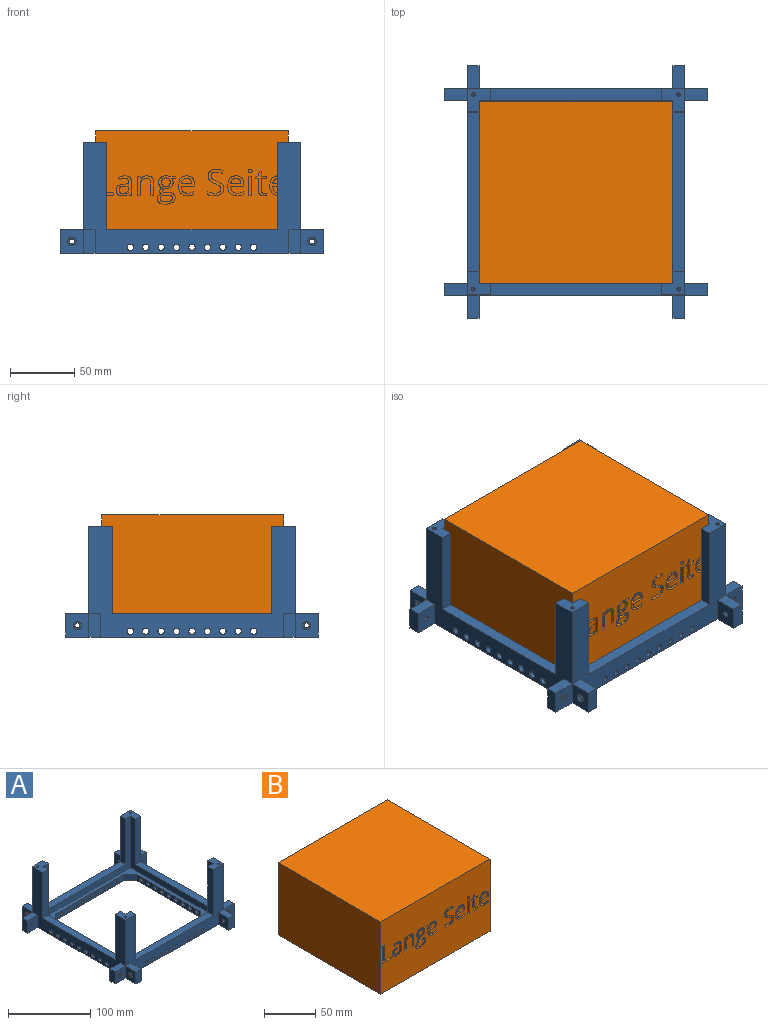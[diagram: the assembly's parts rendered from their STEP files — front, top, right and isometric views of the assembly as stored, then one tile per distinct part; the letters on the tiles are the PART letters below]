
ASSEMBLY  parts=2 mates=1
PART A: 142 faces, bbox 205x196.5x86 mm
  f0: plane 20.61x9mm, normal (0,1,0), area 185.5mm2, adj f1,f16,f33,f129
  f1: plane 142.5x77mm, normal (-1,0,0), area 2417.1mm2, adj f0,f16,f51,f53,f54,f67,f68,f70
  f2: cylinder r=2mm len=7mm, axis (-1,0,0), area 88mm2, adj f27,f90
  f3: cylinder r=2mm len=7mm, axis (0,-1,0), area 88mm2, adj f32,f88
  f4: cylinder r=2mm len=7mm, axis (0,-1,0), area 88mm2, adj f34,f86
  f5: cylinder r=2mm len=7mm, axis (1,0,0), area 88mm2, adj f39,f84
  f6: cylinder r=2mm len=7mm, axis (0,-1,0), area 88mm2, adj f46,f82
  f7: cylinder r=2mm len=7mm, axis (1,0,0), area 88mm2, adj f41,f80
  f8: cylinder r=2mm len=7mm, axis (-1,0,0), area 88mm2, adj f25,f78
  f9: cylinder r=2mm len=7mm, axis (0,-1,0), area 88mm2, adj f48,f76
  f10: plane 133x9mm, normal (0,0,1), area 1197mm2, adj f40,f51,f69,f72
  f11: plane 124.5x9mm, normal (0,0,1), area 1120.5mm2, adj f47,f52,f63,f73
  f12: plane 18x9mm, normal (0,0,1), area 162mm2, adj f44,f45,f46,f47
  f13: plane 18x9mm, normal (0,0,1), area 162mm2, adj f40,f41,f42,f43
  f14: plane 18x9mm, normal (0,0,1), area 162mm2, adj f37,f38,f39,f40
  f15: plane 18x9mm, normal (0,0,1), area 162mm2, adj f33,f34,f35,f36
  f16: plane 124.5x9mm, normal (0,0,1), area 1120.5mm2, adj f0,f1,f33,f70
  f17: plane 133x9mm, normal (0,0,1), area 1197mm2, adj f26,f53,f64,f66
  f18: plane 18x9mm, normal (0,0,1), area 162mm2, adj f30,f31,f32,f33
  f19: plane 18x9mm, normal (0,0,1), area 162mm2, adj f26,f27,f28,f29
  f20: plane 18x9mm, normal (0,0,1), area 162mm2, adj f23,f24,f25,f26
  f21: plane 18x9mm, normal (0,0,1), area 162mm2, adj f22,f47,f48,f49
  f22: plane 18x18mm, normal (0,-1,0), area 290.8mm2, adj f21,f23,f49,f50,f75
  f23: plane 18x18mm, normal (-1,0,0), area 290.8mm2, adj f20,f22,f24,f50,f77
  f24: plane 18x9mm, normal (0,-1,0), area 162mm2, adj f20,f23,f25,f50
  f25: plane 18x18mm, normal (1,0,0), area 311.4mm2, adj f8,f20,f24,f26,f50
  f26: plane 169x86mm, normal (0,-1,0), area 4989.3mm2, adj f17,f19,f20,f25,f27,f33,f47,f50
  f27: plane 18x18mm, normal (-1,0,0), area 311.4mm2, adj f2,f19,f26,f28,f50
  f28: plane 18x9mm, normal (0,-1,0), area 162mm2, adj f19,f27,f29,f50
  f29: plane 18x18mm, normal (1,0,0), area 290.8mm2, adj f19,f28,f30,f50,f89
  f30: plane 18x18mm, normal (0,-1,0), area 290.8mm2, adj f18,f29,f31,f50,f87
  f31: plane 18x9mm, normal (1,0,0), area 162mm2, adj f18,f30,f32,f50
  f32: plane 18x18mm, normal (0,1,0), area 311.4mm2, adj f3,f18,f31,f33,f50
  f33: plane 160.5x86mm, normal (1,0,0), area 4746.9mm2, adj f0,f15,f16,f18,f26,f32,f34,f40
  f34: plane 18x18mm, normal (0,-1,0), area 311.4mm2, adj f4,f15,f33,f35,f50
  f35: plane 18x9mm, normal (1,0,0), area 162mm2, adj f15,f34,f36,f50
  f36: plane 18x18mm, normal (0,1,0), area 290.8mm2, adj f15,f35,f37,f50,f85
  f37: plane 18x18mm, normal (1,0,0), area 290.8mm2, adj f14,f36,f38,f50,f83
  f38: plane 18x9mm, normal (0,1,0), area 162mm2, adj f14,f37,f39,f50
  f39: plane 18x18mm, normal (-1,0,0), area 311.4mm2, adj f5,f14,f38,f40,f50
  f40: plane 169x86mm, normal (0,1,0), area 4989.3mm2, adj f10,f13,f14,f33,f39,f41,f47,f50
  f41: plane 18x18mm, normal (1,0,0), area 311.4mm2, adj f7,f13,f40,f42,f50
  f42: plane 18x9mm, normal (0,1,0), area 162mm2, adj f13,f41,f43,f50
  f43: plane 18x18mm, normal (-1,0,0), area 290.8mm2, adj f13,f42,f44,f50,f79
  f44: plane 18x18mm, normal (0,1,0), area 290.8mm2, adj f12,f43,f45,f50,f81
  f45: plane 18x9mm, normal (-1,0,0), area 162mm2, adj f12,f44,f46,f50
  f46: plane 18x18mm, normal (0,-1,0), area 311.4mm2, adj f6,f12,f45,f47,f50
  f47: plane 160.5x86mm, normal (-1,0,0), area 4836.3mm2, adj f11,f12,f21,f26,f40,f46,f48,f50
  f48: plane 18x18mm, normal (0,1,0), area 311.4mm2, adj f9,f21,f47,f49,f50
  f49: plane 18x9mm, normal (-1,0,0), area 162mm2, adj f21,f22,f48,f50
  f50: plane 205x196.5mm, normal (0,0,-1), area 9989.5mm2, adj f22,f23,f24,f25,f26,f27,f28,f29
  f51: plane 151x77mm, normal (0,-1,0), area 2583mm2, adj f1,f10,f52,f54,f69,f71,f72,f74
  f52: plane 142.5x77mm, normal (1,0,0), area 2506.5mm2, adj f11,f51,f53,f54,f63,f65,f73,f74
  f53: plane 151x77mm, normal (0,1,0), area 2583mm2, adj f1,f17,f52,f54,f64,f65,f66,f68
  f54: plane 151x142.5mm, normal (0,0,1), area 3086.5mm2, adj f1,f51,f52,f53,f55,f56,f57,f58
  f55: plane 11.21x11.21mm, normal (0.71,-0.71,0), area 142.7mm2, adj f50,f54,f56,f62
  f56: plane 110.07x9mm, normal (1,0,0), area 813.9mm2, adj f50,f54,f55,f57,f100,f101,f102,f103
  f57: plane 11.21x11.21mm, normal (0.71,0.71,0), area 142.7mm2, adj f50,f54,f56,f58
  f58: plane 118.57x9mm, normal (0,1,0), area 890.4mm2, adj f50,f54,f57,f59,f118,f119,f120,f121
  f59: plane 11.21x11.21mm, normal (-0.71,0.71,0), area 142.7mm2, adj f50,f54,f58,f60
  f60: plane 110.07x9mm, normal (-1,0,0), area 813.9mm2, adj f50,f54,f59,f61,f91,f92,f93,f94
  f61: plane 11.21x11.21mm, normal (-0.71,-0.71,0), area 142.7mm2, adj f50,f54,f60,f62
  f62: plane 118.57x9mm, normal (0,-1,0), area 890.4mm2, adj f50,f54,f55,f61,f109,f110,f111,f112
  f63: plane 68x9mm, normal (0,1,0), area 612mm2, adj f11,f47,f52,f65
  f64: plane 68x9mm, normal (1,0,0), area 612mm2, adj f17,f26,f53,f65
  f65: plane 18x18mm, normal (0,0,1), area 235.9mm2, adj f26,f47,f52,f53,f63,f64,f131
  f66: plane 68x9mm, normal (-1,0,0), area 612mm2, adj f17,f26,f53,f68
  f67: plane 26.61x9mm, normal (0,1,0), area 239.5mm2, adj f1,f33,f68,f127
  f68: plane 18x18mm, normal (0,0,1), area 235.9mm2, adj f1,f26,f33,f53,f66,f67,f134
  f69: plane 68x9mm, normal (-1,0,0), area 612mm2, adj f10,f40,f51,f71
  f70: plane 68x9mm, normal (0,-1,0), area 612mm2, adj f1,f16,f33,f71
  f71: plane 18x18mm, normal (0,0,1), area 235.9mm2, adj f1,f33,f40,f51,f69,f70,f137
  f72: plane 68x9mm, normal (1,0,0), area 612mm2, adj f10,f40,f51,f74
  f73: plane 68x9mm, normal (0,-1,0), area 612mm2, adj f11,f47,f52,f74
  f74: plane 18x18mm, normal (0,0,1), area 235.9mm2, adj f40,f47,f51,f52,f72,f73,f140
  f75: cylinder r=3.25mm len=6.5mm, axis (0,-1,0), area 40.8mm2, adj f22,f76
  f76: plane 6.5x6.5mm, normal (0,-1,0), area 20.6mm2, adj f9,f75
  f77: cylinder r=3.25mm len=6.5mm, axis (-1,0,0), area 40.8mm2, adj f23,f78
  f78: plane 6.5x6.5mm, normal (-1,0,0), area 20.6mm2, adj f8,f77
  f79: cylinder r=3.25mm len=6.5mm, axis (-1,0,0), area 40.8mm2, adj f43,f80
  f80: plane 6.5x6.5mm, normal (-1,0,0), area 20.6mm2, adj f7,f79
  f81: cylinder r=3.25mm len=6.5mm, axis (0,1,0), area 40.8mm2, adj f44,f82
  f82: plane 6.5x6.5mm, normal (0,1,0), area 20.6mm2, adj f6,f81
  f83: cylinder r=3.25mm len=6.5mm, axis (1,0,0), area 40.8mm2, adj f37,f84
  f84: plane 6.5x6.5mm, normal (1,0,0), area 20.6mm2, adj f5,f83
  f85: cylinder r=3.25mm len=6.5mm, axis (0,1,0), area 40.8mm2, adj f36,f86
  f86: plane 6.5x6.5mm, normal (0,1,0), area 20.6mm2, adj f4,f85
  f87: cylinder r=3.25mm len=6.5mm, axis (0,-1,0), area 40.8mm2, adj f30,f88
  f88: plane 6.5x6.5mm, normal (0,-1,0), area 20.6mm2, adj f3,f87
  f89: cylinder r=3.25mm len=6.5mm, axis (1,0,0), area 40.8mm2, adj f29,f90
  f90: plane 6.5x6.5mm, normal (1,0,0), area 20.6mm2, adj f2,f89
  f91: cylinder r=2.5mm len=14mm, axis (1,0,0), area 219.9mm2, adj f33,f60
  f92: cylinder r=2.5mm len=14mm, axis (1,0,0), area 219.9mm2, adj f33,f60
  f93: cylinder r=2.5mm len=14mm, axis (1,0,0), area 219.9mm2, adj f33,f60
  f94: cylinder r=2.5mm len=14mm, axis (1,0,0), area 219.9mm2, adj f33,f60
  f95: cylinder r=2.5mm len=14mm, axis (1,0,0), area 219.9mm2, adj f33,f60
  f96: cylinder r=2.5mm len=14mm, axis (1,0,0), area 219.9mm2, adj f33,f60
  f97: cylinder r=2.5mm len=14mm, axis (1,0,0), area 219.9mm2, adj f33,f60
  f98: cylinder r=2.5mm len=14mm, axis (1,0,0), area 219.9mm2, adj f33,f60
  f99: cylinder r=2.5mm len=14mm, axis (1,0,0), area 219.9mm2, adj f33,f60
  f100: cylinder r=2.5mm len=14mm, axis (1,0,0), area 219.9mm2, adj f47,f56
  f101: cylinder r=2.5mm len=14mm, axis (1,0,0), area 219.9mm2, adj f47,f56
  f102: cylinder r=2.5mm len=14mm, axis (1,0,0), area 219.9mm2, adj f47,f56
  f103: cylinder r=2.5mm len=14mm, axis (1,0,0), area 219.9mm2, adj f47,f56
  f104: cylinder r=2.5mm len=14mm, axis (1,0,0), area 219.9mm2, adj f47,f56
  f105: cylinder r=2.5mm len=14mm, axis (1,0,0), area 219.9mm2, adj f47,f56
  f106: cylinder r=2.5mm len=14mm, axis (1,0,0), area 219.9mm2, adj f47,f56
  f107: cylinder r=2.5mm len=14mm, axis (1,0,0), area 219.9mm2, adj f47,f56
  f108: cylinder r=2.5mm len=14mm, axis (1,0,0), area 219.9mm2, adj f47,f56
  f109: cylinder r=2.5mm len=14mm, axis (0,-1,0), area 219.9mm2, adj f40,f62
  f110: cylinder r=2.5mm len=14mm, axis (0,-1,0), area 219.9mm2, adj f40,f62
  f111: cylinder r=2.5mm len=14mm, axis (0,-1,0), area 219.9mm2, adj f40,f62
  f112: cylinder r=2.5mm len=14mm, axis (0,-1,0), area 219.9mm2, adj f40,f62
  f113: cylinder r=2.5mm len=14mm, axis (0,-1,0), area 219.9mm2, adj f40,f62
  f114: cylinder r=2.5mm len=14mm, axis (0,-1,0), area 219.9mm2, adj f40,f62
  f115: cylinder r=2.5mm len=14mm, axis (0,-1,0), area 219.9mm2, adj f40,f62
  f116: cylinder r=2.5mm len=14mm, axis (0,-1,0), area 219.9mm2, adj f40,f62
  f117: cylinder r=2.5mm len=14mm, axis (0,-1,0), area 219.9mm2, adj f40,f62
  f118: cylinder r=2.5mm len=14mm, axis (0,-1,0), area 219.9mm2, adj f26,f58
  f119: cylinder r=2.5mm len=14mm, axis (0,-1,0), area 219.9mm2, adj f26,f58
  f120: cylinder r=2.5mm len=14mm, axis (0,-1,0), area 219.9mm2, adj f26,f58
  f121: cylinder r=2.5mm len=14mm, axis (0,-1,0), area 219.9mm2, adj f26,f58
  f122: cylinder r=2.5mm len=14mm, axis (0,-1,0), area 219.9mm2, adj f26,f58
  f123: cylinder r=2.5mm len=14mm, axis (0,-1,0), area 219.9mm2, adj f26,f58
  f124: cylinder r=2.5mm len=14mm, axis (0,-1,0), area 219.9mm2, adj f26,f58
  f125: cylinder r=2.5mm len=14mm, axis (0,-1,0), area 219.9mm2, adj f26,f58
  f126: cylinder r=2.5mm len=14mm, axis (0,-1,0), area 219.9mm2, adj f26,f58
  f127: plane 9x5mm, normal (0,0.5,-0.87), area 52mm2, adj f1,f33,f67,f128
  f128: plane 15x9mm, normal (0,1,0), area 135mm2, adj f1,f33,f127,f129
  f129: plane 9x5mm, normal (0,0.5,0.87), area 52mm2, adj f0,f1,f33,f128
  f130: cylinder r=1.25mm len=11.75mm, axis (0,0,1), area 92.3mm2, adj f131,f132
  f131: cone r=1.25mm half-angle=45deg, axis (0,0,1), area 3.1mm2, adj f65,f130
  f132: cone r=0mm half-angle=59deg, axis (0,0,1), area 5.7mm2, adj f130
  f133: cylinder r=1.25mm len=11.75mm, axis (0,0,1), area 92.3mm2, adj f134,f135
  f134: cone r=1.25mm half-angle=45deg, axis (0,0,1), area 3.1mm2, adj f68,f133
  f135: cone r=0mm half-angle=59deg, axis (0,0,1), area 5.7mm2, adj f133
  f136: cylinder r=1.25mm len=11.75mm, axis (0,0,1), area 92.3mm2, adj f137,f138
  f137: cone r=1.25mm half-angle=45deg, axis (0,0,1), area 3.1mm2, adj f71,f136
  f138: cone r=0mm half-angle=59deg, axis (0,0,1), area 5.7mm2, adj f136
  f139: cylinder r=1.25mm len=11.75mm, axis (0,0,1), area 92.3mm2, adj f140,f141
  f140: cone r=1.25mm half-angle=45deg, axis (0,0,1), area 3.1mm2, adj f74,f139
  f141: cone r=0mm half-angle=59deg, axis (0,0,1), area 5.7mm2, adj f139
PART B: 230 faces, bbox 150x141.5x86 mm
  f0: plane 150x86mm, normal (0,-1,0), area 11875mm2, adj f1,f2,f4,f5,f6,f7,f8,f9
  f1: plane 141.5x86mm, normal (-1,0,0), area 12169mm2, adj f0,f3,f4,f5
  f2: plane 141.5x86mm, normal (1,0,0), area 12169mm2, adj f0,f3,f4,f5
  f3: plane 150x86mm, normal (0,1,0), area 12900mm2, adj f1,f2,f4,f5
  f4: plane 150x141.5mm, normal (0,0,1), area 21225mm2, adj f0,f1,f2,f3
  f5: plane 150x141.5mm, normal (0,0,-1), area 21225mm2, adj f0,f1,f2,f3
  f6: extruded ~3x1.17mm, area 3.5mm2, adj f0,f7,f24,f25
  f7: extruded ~3x1.77mm, area 5.9mm2, adj f0,f6,f8,f25
  f8: extruded ~3x2.08mm, area 6.7mm2, adj f0,f7,f9,f25
  f9: plane 8.84x3mm, normal (-1,0,0), area 26.5mm2, adj f0,f8,f10,f25
  f10: plane 4.36x3mm, normal (0,0,1), area 13.1mm2, adj f0,f9,f11,f25
  f11: plane 3x1.77mm, normal (-1,0,0), area 5.3mm2, adj f0,f10,f12,f25
  f12: plane 4.36x3mm, normal (0,0,-1), area 13.1mm2, adj f0,f11,f13,f25
  f13: plane 3.48x3mm, normal (-1,0,0), area 10.4mm2, adj f0,f12,f14,f25
  f14: plane 3x1.32mm, normal (0,0,-1), area 3.9mm2, adj f0,f13,f15,f25
  f15: plane 3.2x3mm, normal (0.96,0,-0.29), area 10mm2, adj f0,f14,f16,f25
  f16: plane 3x2.15mm, normal (0.4,0,-0.92), area 7.1mm2, adj f0,f15,f17,f25
  f17: plane 3x1.1mm, normal (1,0,0), area 3.3mm2, adj f0,f16,f18,f25
  f18: plane 3x2.15mm, normal (0,0,1), area 6.5mm2, adj f0,f17,f19,f25
  f19: plane 8.93x3mm, normal (1,0,0), area 26.8mm2, adj f0,f18,f20,f25
  f20: extruded ~4.59x4.35mm, area 21.8mm2, adj f0,f19,f21,f25
  f21: extruded ~3x1.3mm, area 3.9mm2, adj f0,f20,f22,f25
  f22: extruded ~3x1.09mm, area 3.4mm2, adj f0,f21,f23,f25
  f23: plane 3x1.74mm, normal (-1,0,0), area 5.2mm2, adj f0,f22,f24,f25
  f24: extruded ~3x0.89mm, area 2.7mm2, adj f0,f6,f23,f25
  f25: plane 18.77x8.89mm, normal (0,-1,0), area 58.3mm2, adj f6,f7,f8,f9,f10,f11,f12,f13
  f26: extruded ~3.34x3mm, area 10.9mm2, adj f27,f52,f53,f225
  f27: extruded ~3x2.09mm, area 6.7mm2, adj f26,f28,f53,f225
  f28: extruded ~3x1.88mm, area 6.3mm2, adj f27,f29,f53,f225
  f29: extruded ~3x2.32mm, area 8.2mm2, adj f28,f30,f53,f225
  f30: extruded ~3.91x3mm, area 12.1mm2, adj f29,f31,f53,f225
  f31: plane 3x2.28mm, normal (-0.04,0,1), area 6.8mm2, adj f30,f32,f53,f225
  f32: plane 3x1.35mm, normal (1,0,0), area 4.1mm2, adj f31,f52,f53,f225
  f33: plane 3x2.14mm, normal (0.98,0,0.21), area 6.6mm2, adj f0,f34,f51,f53
  f34: plane 3x1.69mm, normal (0,0,1), area 5.1mm2, adj f0,f33,f35,f53
  f35: plane 10.25x3mm, normal (-1,0,0), area 30.7mm2, adj f0,f34,f36,f53
  f36: extruded ~3.82x3mm, area 12.5mm2, adj f0,f35,f37,f53
  f37: extruded ~3.98x3mm, area 12.7mm2, adj f0,f36,f38,f53
  f38: extruded ~3x2.65mm, area 8mm2, adj f0,f37,f39,f53
  f39: extruded ~3x2.43mm, area 7.8mm2, adj f0,f38,f40,f53
  f40: plane 3x1.74mm, normal (0.93,0,0.37), area 5.6mm2, adj f0,f39,f41,f53
  f41: extruded ~4.24x3mm, area 13.3mm2, adj f0,f40,f42,f53
  f42: extruded ~3x2.43mm, area 8mm2, adj f0,f41,f43,f53
  f43: extruded ~3x2.61mm, area 8.3mm2, adj f0,f42,f44,f53
  f44: plane 3x0.93mm, normal (1,0,0), area 2.8mm2, adj f0,f43,f45,f53
  f45: plane 3x2.55mm, normal (0.03,0,-1), area 7.6mm2, adj f0,f44,f46,f53
  f46: extruded ~7.27x4.76mm, area 29.3mm2, adj f0,f45,f47,f53
  f47: extruded ~3.27x3mm, area 10.9mm2, adj f0,f46,f48,f53
  f48: extruded ~3.5x3mm, area 11.3mm2, adj f0,f47,f49,f53
  f49: extruded ~3x2.79mm, area 8.6mm2, adj f0,f48,f50,f53
  f50: extruded ~3x2.24mm, area 8.9mm2, adj f0,f49,f51,f53
  f51: plane 3x0.11mm, normal (0,0,1), area 0.3mm2, adj f0,f33,f50,f53
  f52: extruded ~3.26x3mm, area 10.7mm2, adj f26,f32,f53,f225
  f53: plane 15.53x12.04mm, normal (0,-1,0), area 88.3mm2, adj f26,f27,f28,f29,f30,f31,f32,f33
  f54: extruded ~3x2.88mm, area 9.6mm2, adj f55,f72,f73,f226
  f55: extruded ~3x2.74mm, area 9.2mm2, adj f54,f56,f73,f226
  f56: extruded ~3.29x3mm, area 10.5mm2, adj f55,f57,f73,f226
  f57: plane 7.85x3mm, normal (0,0,-1), area 23.6mm2, adj f56,f72,f73,f226
  f58: extruded ~5.25x3mm, area 17.4mm2, adj f0,f59,f71,f73
  f59: extruded ~3x2.6mm, area 7.8mm2, adj f0,f58,f60,f73
  f60: extruded ~3x2.28mm, area 7.2mm2, adj f0,f59,f61,f73
  f61: plane 3x2.03mm, normal (-1,0,0), area 6.1mm2, adj f0,f60,f62,f73
  f62: extruded ~4.79x3mm, area 14.8mm2, adj f0,f61,f63,f73
  f63: extruded ~3.57x3mm, area 11.8mm2, adj f0,f62,f64,f73
  f64: extruded ~4.01x3mm, area 13mm2, adj f0,f63,f65,f73
  f65: plane 10.34x3mm, normal (0,0,1), area 31mm2, adj f0,f64,f66,f73
  f66: plane 3x1.44mm, normal (-1,0,0), area 4.3mm2, adj f0,f65,f67,f73
  f67: extruded ~4.9x3mm, area 15.9mm2, adj f0,f66,f68,f73
  f68: extruded ~4.46x3mm, area 15mm2, adj f0,f67,f69,f73
  f69: extruded ~4.8x3mm, area 16.3mm2, adj f0,f68,f70,f73
  f70: extruded ~5.77x3mm, area 18.5mm2, adj f0,f69,f71,f73
  f71: extruded ~5.63x3mm, area 18.3mm2, adj f0,f58,f70,f73
  f72: extruded ~3.26x3mm, area 10.7mm2, adj f54,f57,f73,f226
  f73: plane 15.56x12.7mm, normal (0,-1,0), area 89.9mm2, adj f54,f55,f56,f57,f58,f59,f60,f61
  f74: extruded ~3x2.88mm, area 9.6mm2, adj f75,f92,f93,f227
  f75: extruded ~3x2.74mm, area 9.2mm2, adj f74,f76,f93,f227
  f76: extruded ~3.29x3mm, area 10.5mm2, adj f75,f77,f93,f227
  f77: plane 7.85x3mm, normal (0,0,-1), area 23.6mm2, adj f76,f92,f93,f227
  f78: extruded ~5.25x3mm, area 17.4mm2, adj f0,f79,f91,f93
  f79: extruded ~3x2.6mm, area 7.8mm2, adj f0,f78,f80,f93
  f80: extruded ~3x2.28mm, area 7.2mm2, adj f0,f79,f81,f93
  f81: plane 3x2.03mm, normal (-1,0,0), area 6.1mm2, adj f0,f80,f82,f93
  f82: extruded ~4.79x3mm, area 14.8mm2, adj f0,f81,f83,f93
  f83: extruded ~3.57x3mm, area 11.8mm2, adj f0,f82,f84,f93
  f84: extruded ~4.01x3mm, area 13mm2, adj f0,f83,f85,f93
  f85: plane 10.34x3mm, normal (0,0,1), area 31mm2, adj f0,f84,f86,f93
  f86: plane 3x1.44mm, normal (-1,0,0), area 4.3mm2, adj f0,f85,f87,f93
  f87: extruded ~4.9x3mm, area 15.9mm2, adj f0,f86,f88,f93
  f88: extruded ~4.46x3mm, area 15mm2, adj f0,f87,f89,f93
  f89: extruded ~4.8x3mm, area 16.3mm2, adj f0,f88,f90,f93
  f90: extruded ~5.77x3mm, area 18.5mm2, adj f0,f89,f91,f93
  f91: extruded ~5.63x3mm, area 18.3mm2, adj f0,f78,f90,f93
  f92: extruded ~3.26x3mm, area 10.7mm2, adj f74,f77,f93,f227
  f93: plane 15.56x12.7mm, normal (0,-1,0), area 89.9mm2, adj f74,f75,f76,f77,f78,f79,f80,f81
  f94: extruded ~3x1.14mm, area 3.7mm2, adj f0,f95,f101,f102
  f95: extruded ~3x1.14mm, area 3.7mm2, adj f0,f94,f96,f102
  f96: extruded ~3x0.96mm, area 3.2mm2, adj f0,f95,f97,f102
  f97: extruded ~3x0.94mm, area 3.1mm2, adj f0,f96,f98,f102
  f98: extruded ~3x1.14mm, area 3.7mm2, adj f0,f97,f99,f102
  f99: extruded ~3x1.14mm, area 3.7mm2, adj f0,f98,f100,f102
  f100: extruded ~3x0.94mm, area 3.1mm2, adj f0,f99,f101,f102
  f101: extruded ~3x0.96mm, area 3.2mm2, adj f0,f94,f100,f102
  f102: plane 3.03x2.69mm, normal (0,-1,0), area 6.6mm2, adj f94,f95,f96,f97,f98,f99,f100,f101
  f103: plane 3x2.28mm, normal (0,0,1), area 6.8mm2, adj f0,f104,f106,f107
  f104: plane 15.01x3mm, normal (-1,0,0), area 45mm2, adj f0,f103,f105,f107
  f105: plane 3x2.28mm, normal (0,0,-1), area 6.8mm2, adj f0,f104,f106,f107
  f106: plane 15.01x3mm, normal (1,0,0), area 45mm2, adj f0,f103,f105,f107
  f107: plane 15.01x2.28mm, normal (0,-1,0), area 34.2mm2, adj f103,f104,f105,f106
  f108: extruded ~4.12x3mm, area 14.2mm2, adj f0,f109,f132,f133
  f109: extruded ~3.34x3mm, area 10.9mm2, adj f0,f108,f110,f133
  f110: extruded ~4.34x3mm, area 15mm2, adj f0,f109,f111,f133
  f111: extruded ~3x2.79mm, area 9.1mm2, adj f0,f110,f112,f133
  f112: extruded ~3x1.3mm, area 5.4mm2, adj f0,f111,f113,f133
  f113: extruded ~3x1.71mm, area 5.3mm2, adj f0,f112,f114,f133
  f114: extruded ~3x2.2mm, area 7.6mm2, adj f0,f113,f115,f133
  f115: extruded ~3x2.89mm, area 9.2mm2, adj f0,f114,f116,f133
  f116: extruded ~4.82x3mm, area 14.9mm2, adj f0,f115,f117,f133
  f117: plane 3x2.03mm, normal (-0.94,0,0.34), area 6.5mm2, adj f0,f116,f118,f133
  f118: extruded ~5.49x3mm, area 16.9mm2, adj f0,f117,f119,f133
  f119: extruded ~4.6x3mm, area 14.7mm2, adj f0,f118,f120,f133
  f120: extruded ~3.68x3mm, area 12.7mm2, adj f0,f119,f121,f133
  f121: extruded ~3.57x3mm, area 11.6mm2, adj f0,f120,f122,f133
  f122: extruded ~3.99x3mm, area 14.1mm2, adj f0,f121,f123,f133
  f123: extruded ~3x2.98mm, area 9.7mm2, adj f0,f122,f124,f133
  f124: extruded ~3x1.4mm, area 5.6mm2, adj f0,f123,f125,f133
  f125: extruded ~3x1.7mm, area 5.3mm2, adj f0,f124,f126,f133
  f126: extruded ~3x2.46mm, area 8.5mm2, adj f0,f125,f127,f133
  f127: extruded ~3.51x3mm, area 11mm2, adj f0,f126,f128,f133
  f128: extruded ~3x2.88mm, area 8.7mm2, adj f0,f127,f129,f133
  f129: extruded ~3x2.69mm, area 8.4mm2, adj f0,f128,f130,f133
  f130: plane 3x2.24mm, normal (1,0,0), area 6.7mm2, adj f0,f129,f131,f133
  f131: extruded ~5.48x3mm, area 16.8mm2, adj f0,f130,f132,f133
  f132: extruded ~5.21x3mm, area 16.5mm2, adj f0,f108,f131,f133
  f133: plane 20.59x12.6mm, normal (0,-1,0), area 92.8mm2, adj f108,f109,f110,f111,f112,f113,f114,f115
  f134: plane 9.71x3mm, normal (1,0,0), area 29.1mm2, adj f0,f135,f150,f151
  f135: plane 3x2.28mm, normal (0,0,1), area 6.8mm2, adj f0,f134,f136,f151
  f136: plane 9.79x3mm, normal (-1,0,0), area 29.4mm2, adj f0,f135,f137,f151
  f137: extruded ~4.19x3mm, area 13.6mm2, adj f0,f136,f138,f151
  f138: extruded ~4.08x3mm, area 13.2mm2, adj f0,f137,f139,f151
  f139: extruded ~3x2.81mm, area 8.7mm2, adj f0,f138,f140,f151
  f140: extruded ~3x1.96mm, area 7.9mm2, adj f0,f139,f141,f151
  f141: plane 3x0.11mm, normal (0,0,-1), area 0.3mm2, adj f0,f140,f142,f151
  f142: plane 3x2.06mm, normal (-0.98,0,-0.18), area 6.3mm2, adj f0,f141,f143,f151
  f143: plane 3x1.85mm, normal (0,0,-1), area 5.5mm2, adj f0,f142,f144,f151
  f144: plane 15.01x3mm, normal (1,0,0), area 45mm2, adj f0,f143,f145,f151
  f145: plane 3x2.28mm, normal (0,0,1), area 6.8mm2, adj f0,f144,f146,f151
  f146: plane 7.88x3mm, normal (-1,0,0), area 23.6mm2, adj f0,f145,f147,f151
  f147: extruded ~4.21x3mm, area 13.3mm2, adj f0,f146,f148,f151
  f148: extruded ~3.45x3mm, area 11.4mm2, adj f0,f147,f149,f151
  f149: extruded ~3x2.62mm, area 8.6mm2, adj f0,f148,f150,f151
  f150: extruded ~3x2.74mm, area 8.8mm2, adj f0,f134,f149,f151
  f151: plane 15.29x12.55mm, normal (0,-1,0), area 81.7mm2, adj f134,f135,f136,f137,f138,f139,f140,f141
  f152: extruded ~3x2.88mm, area 9.6mm2, adj f153,f170,f171,f228
  f153: extruded ~3x2.74mm, area 9.2mm2, adj f152,f154,f171,f228
  f154: extruded ~3.29x3mm, area 10.5mm2, adj f153,f155,f171,f228
  f155: plane 7.85x3mm, normal (0,0,-1), area 23.6mm2, adj f154,f170,f171,f228
  f156: extruded ~5.25x3mm, area 17.4mm2, adj f0,f157,f169,f171
  f157: extruded ~3x2.6mm, area 7.8mm2, adj f0,f156,f158,f171
  f158: extruded ~3x2.28mm, area 7.2mm2, adj f0,f157,f159,f171
  f159: plane 3x2.03mm, normal (-1,0,0), area 6.1mm2, adj f0,f158,f160,f171
  f160: extruded ~4.79x3mm, area 14.8mm2, adj f0,f159,f161,f171
  f161: extruded ~3.57x3mm, area 11.8mm2, adj f0,f160,f162,f171
  f162: extruded ~4.01x3mm, area 13mm2, adj f0,f161,f163,f171
  f163: plane 10.34x3mm, normal (0,0,1), area 31mm2, adj f0,f162,f164,f171
  f164: plane 3x1.44mm, normal (-1,0,0), area 4.3mm2, adj f0,f163,f165,f171
  f165: extruded ~4.9x3mm, area 15.9mm2, adj f0,f164,f166,f171
  f166: extruded ~4.46x3mm, area 15mm2, adj f0,f165,f167,f171
  f167: extruded ~4.8x3mm, area 16.3mm2, adj f0,f166,f168,f171
  f168: extruded ~5.77x3mm, area 18.5mm2, adj f0,f167,f169,f171
  f169: extruded ~5.63x3mm, area 18.3mm2, adj f0,f156,f168,f171
  f170: extruded ~3.26x3mm, area 10.7mm2, adj f152,f155,f171,f228
  f171: plane 15.56x12.7mm, normal (0,-1,0), area 89.9mm2, adj f152,f153,f154,f155,f156,f157,f158,f159
  f172: extruded ~3x2.38mm, area 7.9mm2, adj f173,f215,f216,f229
  f173: extruded ~3x2.56mm, area 8.3mm2, adj f172,f174,f216,f229
  f174: extruded ~3x2.47mm, area 8.1mm2, adj f173,f175,f216,f229
  f175: extruded ~3.38x3.37mm, area 16.4mm2, adj f174,f176,f216,f229
  f176: extruded ~3.33x3.23mm, area 16mm2, adj f175,f215,f216,f229
  f177: extruded ~3x1.85mm, area 6.7mm2, adj f178,f213,f216,f217
  f178: extruded ~3x2.12mm, area 7.1mm2, adj f177,f179,f216,f217
  f179: extruded ~3x2.41mm, area 7.7mm2, adj f178,f180,f216,f217
  f180: plane 3x2.73mm, normal (0,0,1), area 8.2mm2, adj f179,f181,f216,f217
  f181: extruded ~3x2.83mm, area 8.7mm2, adj f180,f182,f216,f217
  f182: extruded ~3x1.69mm, area 5.8mm2, adj f181,f183,f216,f217
  f183: extruded ~3x2.32mm, area 8.5mm2, adj f182,f184,f216,f217
  f184: extruded ~4.24x3mm, area 13.1mm2, adj f183,f213,f216,f217
  f185: plane 3x1.44mm, normal (-1,0,0), area 4.3mm2, adj f0,f186,f214,f216
  f186: plane 5.19x3mm, normal (0,0,-1), area 15.6mm2, adj f0,f185,f187,f216
  f187: extruded ~3x2.13mm, area 6.5mm2, adj f0,f186,f188,f216
  f188: extruded ~4.19x3mm, area 13.5mm2, adj f0,f187,f189,f216
  f189: extruded ~3.8x3mm, area 12.6mm2, adj f0,f188,f190,f216
  f190: extruded ~3x2.63mm, area 8.3mm2, adj f0,f189,f191,f216
  f191: extruded ~3x1.9mm, area 7.6mm2, adj f0,f190,f192,f216
  f192: extruded ~3x1.39mm, area 5.5mm2, adj f0,f191,f193,f216
  f193: extruded ~3x1.44mm, area 4.6mm2, adj f0,f192,f194,f216
  f194: extruded ~3x1.28mm, area 4.1mm2, adj f0,f193,f195,f216
  f195: extruded ~3x0.96mm, area 3.8mm2, adj f0,f194,f196,f216
  f196: extruded ~3x2.46mm, area 8.6mm2, adj f0,f195,f197,f216
  f197: extruded ~3x2.37mm, area 7.8mm2, adj f0,f196,f198,f216
  f198: extruded ~3.1x3mm, area 10.9mm2, adj f0,f197,f199,f216
  f199: extruded ~4.54x3mm, area 14.2mm2, adj f0,f198,f200,f216
  f200: extruded ~5.83x3mm, area 18.2mm2, adj f0,f199,f201,f216
  f201: extruded ~3.8x3mm, area 13.5mm2, adj f0,f200,f202,f216
  f202: extruded ~3x2.99mm, area 10.1mm2, adj f0,f201,f203,f216
  f203: extruded ~3.75x3mm, area 11.9mm2, adj f0,f202,f204,f216
  f204: plane 3x2.66mm, normal (0,0,-1), area 8mm2, adj f0,f203,f205,f216
  f205: extruded ~3x1.74mm, area 5.3mm2, adj f0,f204,f206,f216
  f206: extruded ~3x0.91mm, area 3.3mm2, adj f0,f205,f207,f216
  f207: extruded ~3x1.93mm, area 7.6mm2, adj f0,f206,f208,f216
  f208: extruded ~3x1.26mm, area 3.8mm2, adj f0,f207,f209,f216
  f209: extruded ~4.14x3mm, area 13.3mm2, adj f0,f208,f210,f216
  f210: extruded ~3.52x3mm, area 11.9mm2, adj f0,f209,f211,f216
  f211: extruded ~3x1.74mm, area 5.3mm2, adj f0,f210,f212,f216
  f212: extruded ~3x1.25mm, area 4.3mm2, adj f0,f211,f214,f216
  f213: extruded ~3x2.94mm, area 9.1mm2, adj f177,f184,f216,f217
  f214: plane 3x2.78mm, normal (-0.12,0,0.99), area 8.4mm2, adj f0,f185,f212,f216
  f215: extruded ~3x2.48mm, area 8mm2, adj f172,f176,f216,f229
  f216: plane 22.03x14.16mm, normal (0,-1,0), area 129.1mm2, adj f172,f173,f174,f175,f176,f177,f178,f179
  f217: plane 9.59x5.34mm, normal (0,-1,0), area 43.7mm2, adj f177,f178,f179,f180,f181,f182,f183,f184
  f218: plane 20.03x3mm, normal (1,0,0), area 60.1mm2, adj f0,f219,f223,f224
  f219: plane 11.16x3mm, normal (0,0,1), area 33.5mm2, adj f0,f218,f220,f224
  f220: plane 3x2.11mm, normal (-1,0,0), area 6.3mm2, adj f0,f219,f221,f224
  f221: plane 8.84x3mm, normal (0,0,-1), area 26.5mm2, adj f0,f220,f222,f224
  f222: plane 17.92x3mm, normal (-1,0,0), area 53.8mm2, adj f0,f221,f223,f224
  f223: plane 3x2.33mm, normal (0,0,-1), area 7mm2, adj f0,f218,f222,f224
  f224: plane 20.03x11.16mm, normal (0,-1,0), area 65.2mm2, adj f218,f219,f220,f221,f222,f223
  f225: plane 7.38x5.78mm, normal (0,-1,0), area 34.4mm2, adj f26,f27,f28,f29,f30,f31,f32,f52
  f226: plane 7.85x4.44mm, normal (0,-1,0), area 28.1mm2, adj f54,f55,f56,f57,f72
  f227: plane 7.85x4.44mm, normal (0,-1,0), area 28.1mm2, adj f74,f75,f76,f77,f92
  f228: plane 7.85x4.44mm, normal (0,-1,0), area 28.1mm2, adj f152,f153,f154,f155,f170
  f229: plane 6.7x6.61mm, normal (0,-1,0), area 36.8mm2, adj f172,f173,f174,f175,f176,f215
PLACE A t=(-50.66,-29.46,3.44)mm
PLACE B t=(-41.16,-20.46,12.44)mm fixed
MATE fastened B.f5 <-> A.f54  axis (0,0,-1) through (33.84,-20.46,12.44)mm
